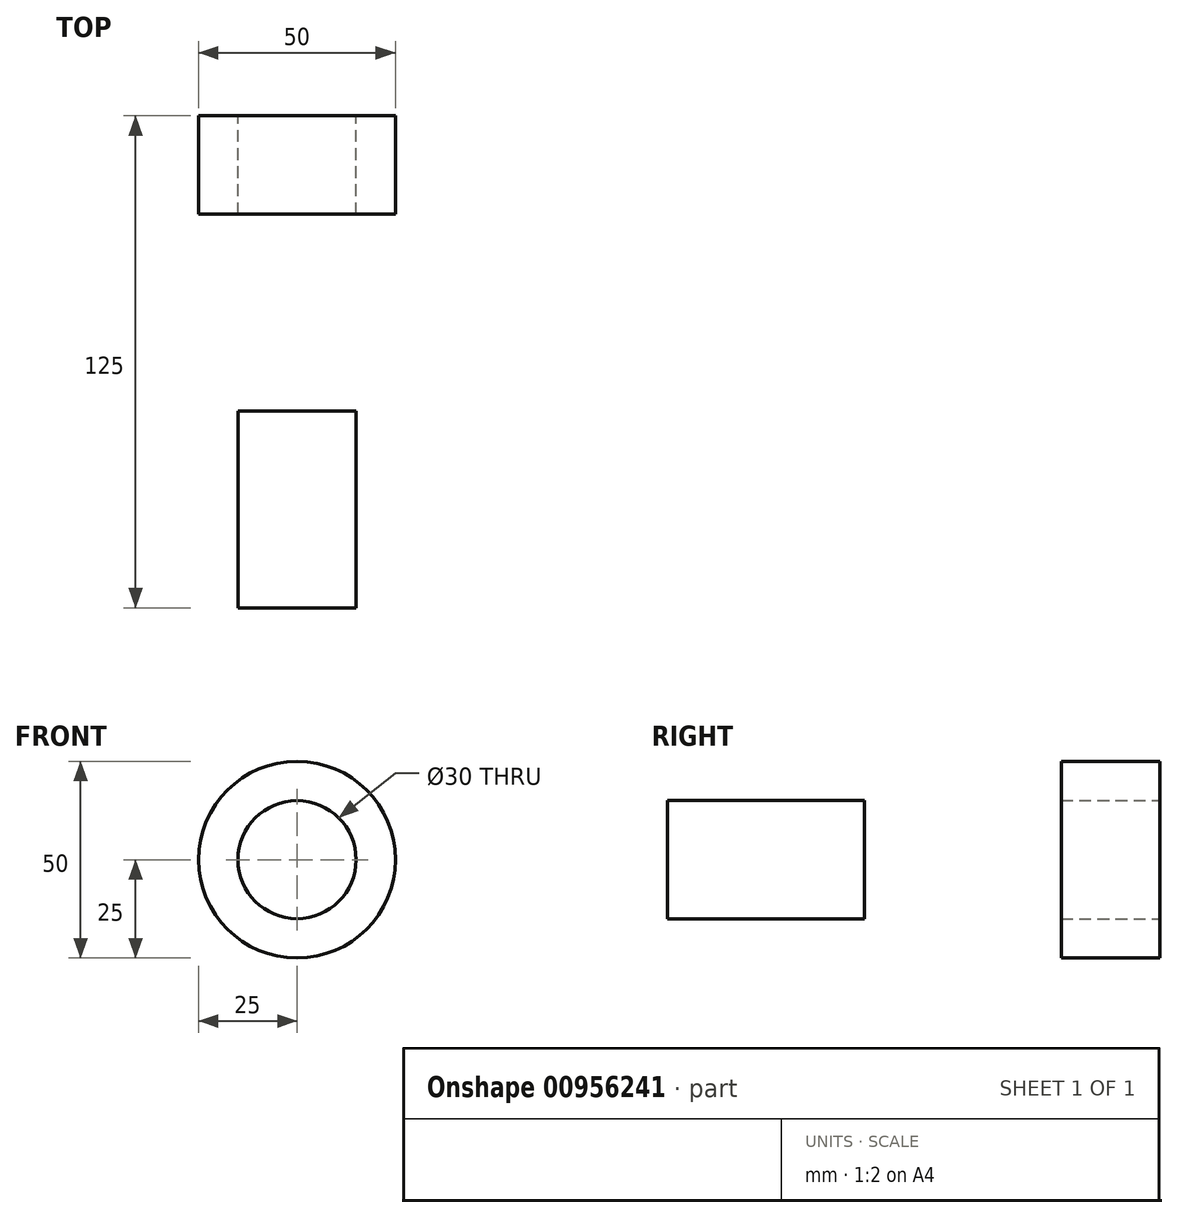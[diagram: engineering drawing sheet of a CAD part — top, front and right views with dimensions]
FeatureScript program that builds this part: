
annotation { "Feature Type Name" : "Feature", "Feature Type Description" : "" }
export const myFeature = defineFeature(function(context is Context, id is Id, definition is map)
    precondition{}
    {
        {
            var Q0;
            Q0=qCreatedBy(makeId("Front.planeOp"),FACE);
            var sketch = newSketch(context, id + "F0", { "sketchPlane" : qUnion([Q0])});
            skCircle(sketch, "E0", {"center": v(0, 0) * mm, "radius": 25 * mm});
            skCircle(sketch, "E1", {"center": v(0, 0) * mm, "radius": 15 * mm});
            skSolve(sketch);
        }
        {
            var Q0;
            Q0=makeQuery(id+"F0.imprint","IMPRINT",FACE,{"disambiguationData":[TD([[makeQuery(id+"F0.imprint","IMPRINT",EDGE,{"derivedFrom":sQuery(id+"F0.wireOp",EDGE,"E0")}),1.0]])]});
            extrude(context, id + "F1", {"entities" : qUnion([Q0]), "depth" : 25 * mm, "offsetDistance" : 25 * mm});
        }
        {
            var Q0;
            Q0=makeQuery(id+"F1.opExtrude","CAP_FACE",FACE,{"disambiguationData":[OSD([sQuery(id+"F0.wireOp",EDGE,"E0"),sQuery(id+"F0.wireOp",EDGE,"E1")])],"isStart":false});
            cPlane(context, id + "F2", {"entities" : qUnion([Q0]), "cplaneType" : CPlaneType.OFFSET, "offset" : 50 * mm, "width" : 150 * mm, "height" : 150 * mm});
        }
        {
            var Q0;
            Q0=qCreatedBy(id+"F2.planeOp",FACE);
            var sketch = newSketch(context, id + "F3", { "sketchPlane" : qUnion([Q0])});
            skCircle(sketch, "E2", {"center": v(0, 0) * mm, "radius": 15 * mm});
            skSolve(sketch);
        }
        {
            var Q0;
            Q0=makeQuery(id+"F3.imprint","IMPRINT",FACE,{"disambiguationData":[TD([[makeQuery(id+"F3.imprint","IMPRINT",EDGE,{"derivedFrom":sQuery(id+"F3.wireOp",EDGE,"E2")}),1.0]])]});
            extrude(context, id + "F4", {"entities" : qUnion([Q0]), "depth" : 50 * mm, "offsetDistance" : 25 * mm});
        }
    });
